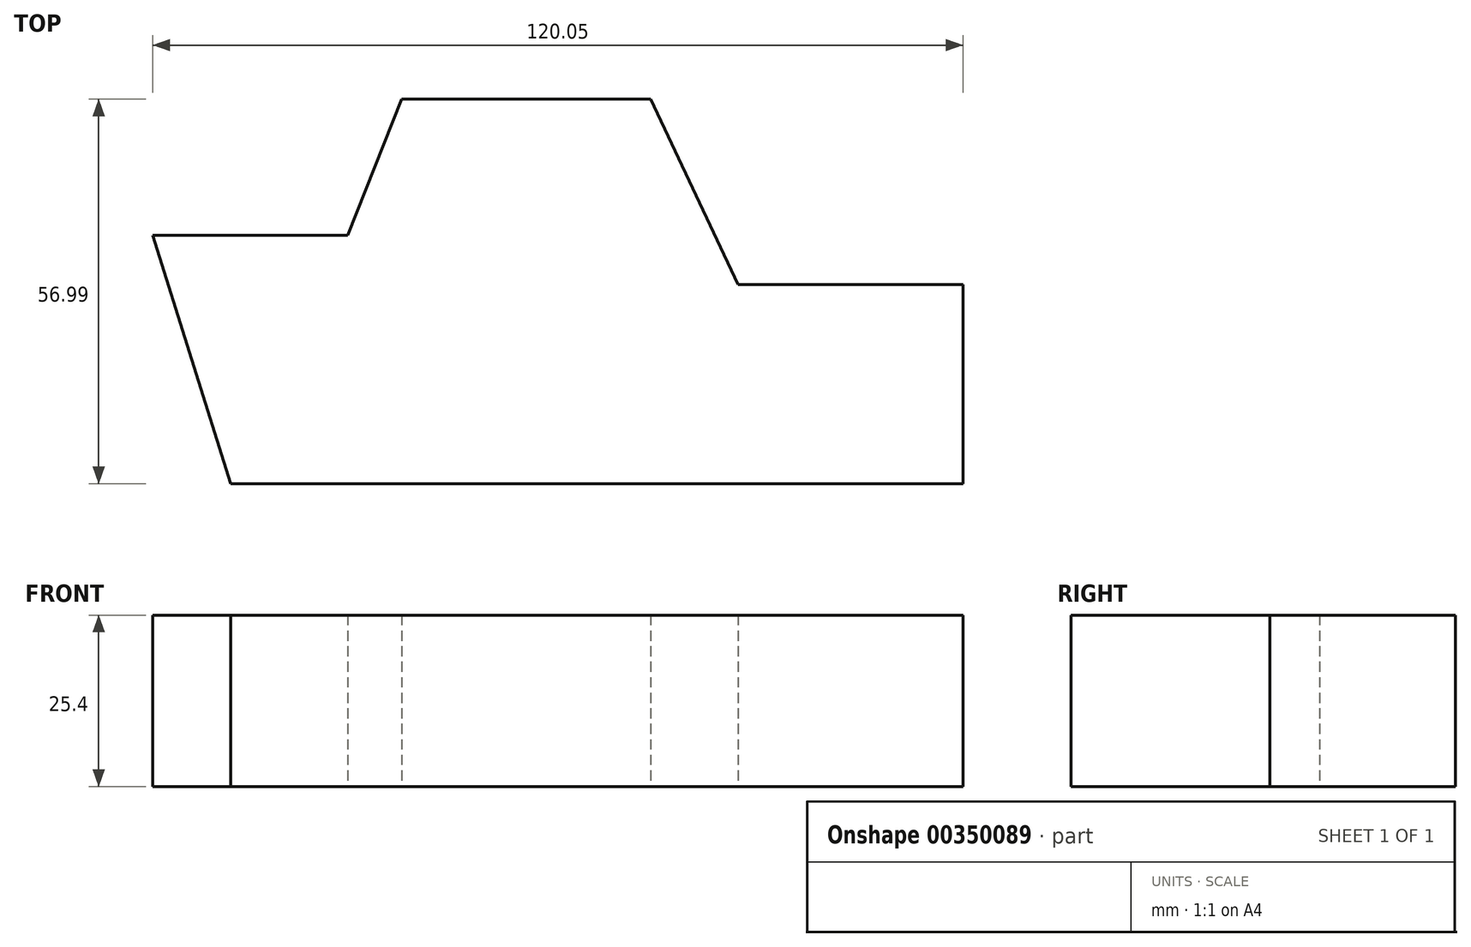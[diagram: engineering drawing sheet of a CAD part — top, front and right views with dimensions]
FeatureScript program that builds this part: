
annotation { "Feature Type Name" : "Feature", "Feature Type Description" : "" }
export const myFeature = defineFeature(function(context is Context, id is Id, definition is map)
    precondition{}
    {
        {
            var Q0;
            Q0=qCreatedBy(makeId("Top.planeOp"),FACE);
            var sketch = newSketch(context, id + "F0", { "sketchPlane" : qUnion([Q0])});
            skLineSegment(sketch, "E0", {"start": v(-51, -45.26) * mm, "end": v(-16.9, -45.26) * mm});
            skLineSegment(sketch, "E1", {"start": v(-16.9, -45.26) * mm, "end": v(57.5, -45.26) * mm});
            skLineSegment(sketch, "E2", {"start": v(57.5, -45.26) * mm, "end": v(57.5, -15.77) * mm});
            skLineSegment(sketch, "E3", {"start": v(57.5, -15.77) * mm, "end": v(24.14, -15.77) * mm});
            skLineSegment(sketch, "E4", {"start": v(24.14, -15.77) * mm, "end": v(11.2, 11.73) * mm});
            skLineSegment(sketch, "E5", {"start": v(11.2, 11.73) * mm, "end": v(-25.67, 11.73) * mm});
            skLineSegment(sketch, "E6", {"start": v(-25.67, 11.73) * mm, "end": v(-33.7, -8.44) * mm});
            skLineSegment(sketch, "E7", {"start": v(-33.7, -8.44) * mm, "end": v(-62.56, -8.44) * mm});
            skLineSegment(sketch, "E8", {"start": v(-62.56, -8.44) * mm, "end": v(-51, -45.26) * mm});
            skSolve(sketch);
        }
        {
            var Q0;
            Q0=makeQuery(id+"F0.imprint","IMPRINT",FACE,{"disambiguationData":[TD([[makeQuery(id+"F0.imprint","IMPRINT",EDGE,{"derivedFrom":sQuery(id+"F0.wireOp",EDGE,"E0")}),1.0]])]});
            extrude(context, id + "F1", {"entities" : qUnion([Q0]), "depth" : 25.4 * mm});
        }
    });
